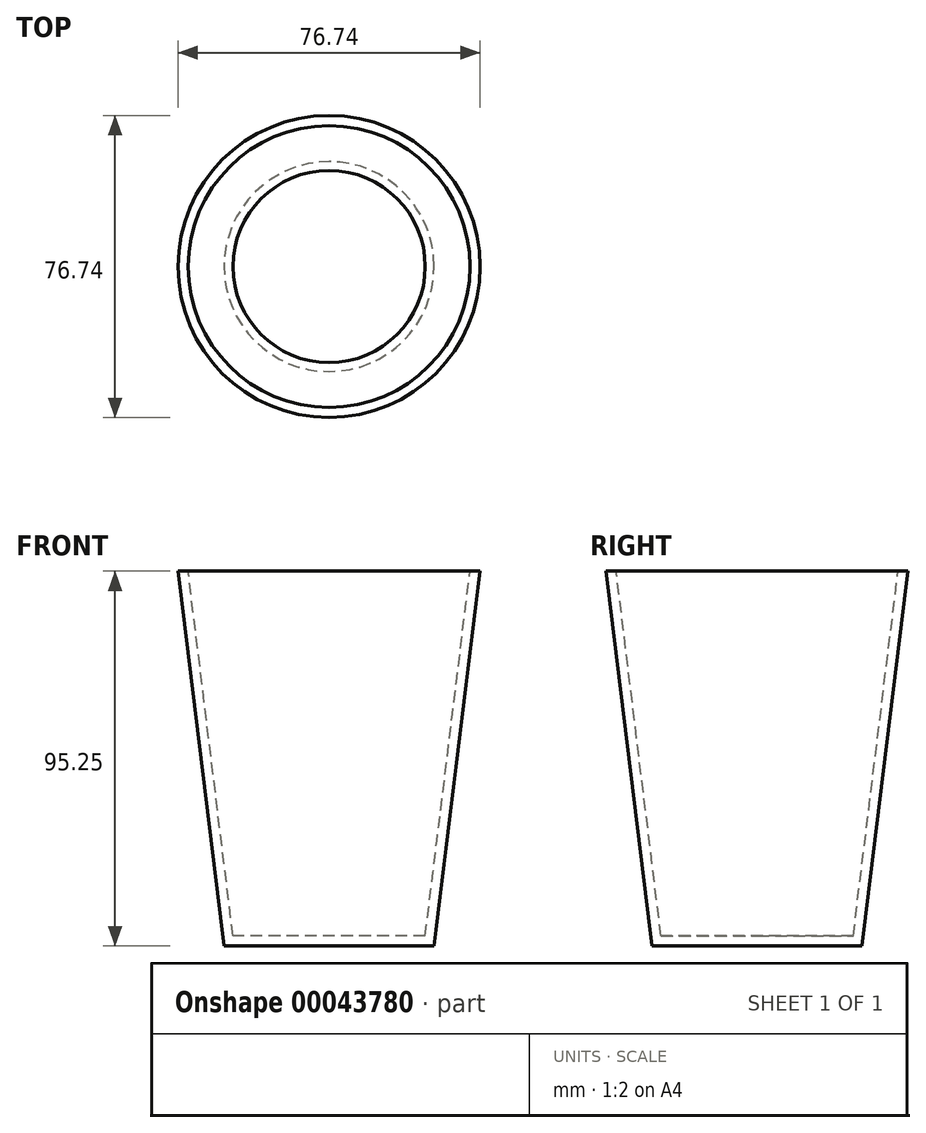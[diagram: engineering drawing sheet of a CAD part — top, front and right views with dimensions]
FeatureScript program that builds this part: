
annotation { "Feature Type Name" : "Feature", "Feature Type Description" : "" }
export const myFeature = defineFeature(function(context is Context, id is Id, definition is map)
    precondition{}
    {
        {
            var Q0;
            Q0=qCreatedBy(makeId("Top.planeOp"),FACE);
            var sketch = newSketch(context, id + "F0", { "sketchPlane" : qUnion([Q0])});
            skCircle(sketch, "E0", {"center": v(0, 0) * mm, "radius": 26.67 * mm});
            skSolve(sketch);
        }
        {
            var Q0;
            Q0=makeQuery(id+"F0.imprint","IMPRINT",FACE,{"disambiguationData":[TD([[makeQuery(id+"F0.imprint","IMPRINT",EDGE,{"derivedFrom":sQuery(id+"F0.wireOp",EDGE,"E0")}),1.0]])]});
            var Q1;
            Q1=sQuery(id+"F0.wireOp",EDGE,"E0");
            extrude(context, id + "F1", {"entities" : qUnion([Q0]), "surfaceEntities" : qUnion([Q1]), "depth" : 95.25 * mm, "hasDraft" : true, "draftAngle" : 7 * degree});
        }
        {
            var Q0;
            Q0=makeQuery(id+"F1.opExtrude","CAP_FACE",FACE,{"disambiguationData":[OSD([sQuery(id+"F0.wireOp",EDGE,"E0")])],"isStart":false});
            shell(context, id + "F2", {"entities" : qUnion([Q0]), "thickness" : 2.54 * mm});
        }
    });
